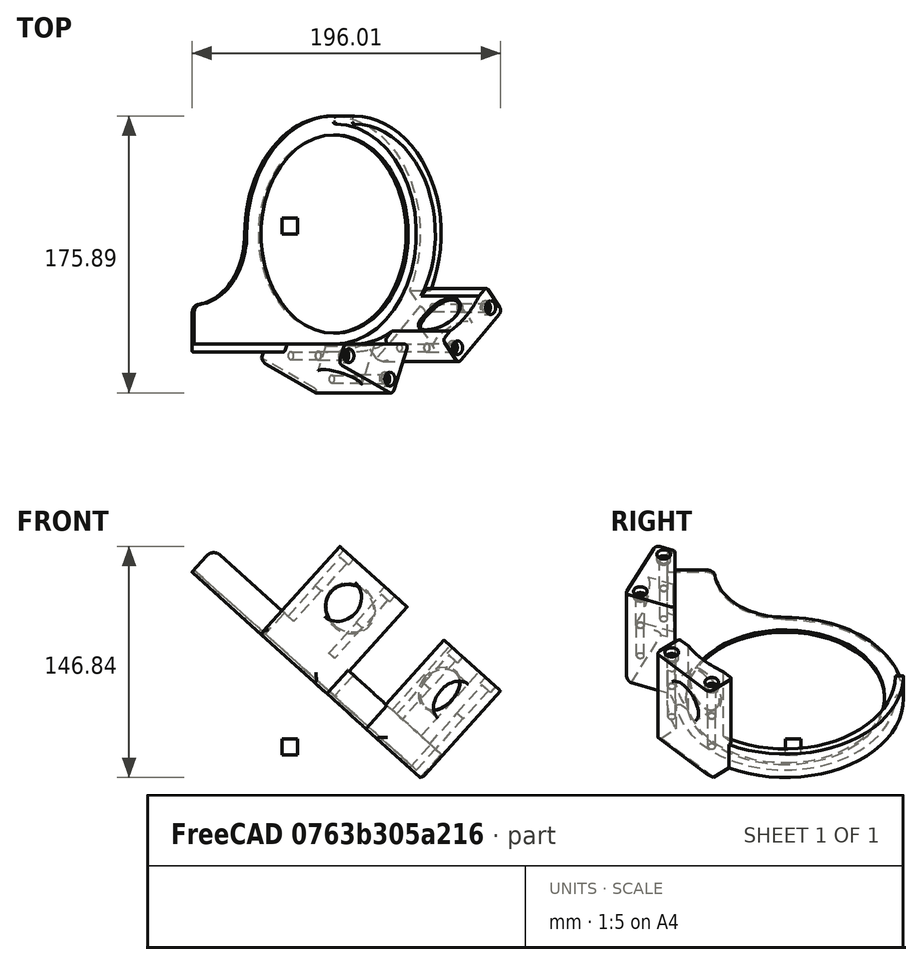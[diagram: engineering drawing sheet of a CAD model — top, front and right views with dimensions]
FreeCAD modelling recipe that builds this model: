
FCSTD DOCUMENT  (FreeCAD 0.19R)
Label: WhiteBike4
License: All rights reserved
LicenseURL: http://en.wikipedia.org/wiki/All_rights_reserved
objects: Sketcher::SketchObject×9, PartDesign::Fillet×7, PartDesign::Pocket×6, PartDesign::Pad×2, Mesh::Feature×2, PartDesign::Chamfer×1, PartDesign::Body×1, Part::Box×1
note: 43 computed .brp shape members not serialized (recipe doc carries the construction recipe); baked Part::Feature solids carry a one-line shape summary decoded from their .brp

FEATURE [Sketcher::SketchObject] Sketch
  FullyConstrained = true
  MapMode = 5
  Placement = pos=(45.5009,-1.12e-14,50.5338) rot=(0.93358,0,-0.358368;3.14159rad)
  sketch-geometry (5):
    g0: Circle CenterX=0 CenterY=0 CenterZ=0 NormalX=0 NormalY=0 NormalZ=1 AngleXU=0 Radius=63
    g1: ArcOfCircle CenterX=0 CenterY=0 CenterZ=0 NormalX=0 NormalY=0 NormalZ=1 AngleXU=0 Radius=75 StartAngle=3.14159 EndAngle=7.85398
    g2: LineSegment StartX=2.3e-14 StartY=75 StartZ=0 EndX=-120 EndY=75 EndZ=0
    g3: LineSegment StartX=-120 StartY=75 StartZ=0 EndX=-120 EndY=45 EndZ=0
    g4: ArcOfCircle CenterX=-120 CenterY=5.5e-15 CenterZ=0 NormalX=0 NormalY=0 NormalZ=1 AngleXU=0 Radius=45 StartAngle=0 EndAngle=1.5708
  constraints (14):
    c: Coincident(g0,g-1)
    c: Coincident(g1,g0)
    c: PointOnObject(g1,g-2)
    c: Coincident(g2,g1)
    c: Horizontal(g2)
    c: Coincident(g2,g3)
    c: Vertical(g3)
    c: Coincident(g4,g3)
    c: Tangent(g1,g4) = 1.5708
    c: Distance(g2) = 120
    c: Perpendicular(g4,g3)
    c: Radius(g0) = 63
    c: Radius(g1) = 75
    c: PointOnObject(g1,g-1)
FEATURE [PartDesign::Pad] Pad
  Direction = (1,1,1)
  Length = 20
  Length2 = 100
  Placement = pos=(45.5009,-1.12e-14,50.5338) rot=(0.93358,0,-0.358368;3.14159rad)
  Profile = -> Sketch
  Type = 0
FEATURE [Sketcher::SketchObject] Sketch002
  FullyConstrained = false
  MapMode = 5
  Placement = pos=(45.5009,-1.12e-14,50.5338) rot=(0,1,0;0.733038rad)
  Support = -> [Pad]
  sketch-geometry (10):
    g0: LineSegment StartX=0 StartY=0 StartZ=0 EndX=200.739 EndY=-222.943 EndZ=0
    g1: LineSegment StartX=-78.1462 StartY=-184.101 StartZ=0 EndX=0 EndY=0 EndZ=0
    g2: LineSegment StartX=-16.0605 StartY=-101.819 StartZ=0 EndX=-62.0857 EndY=-82.2822 EndZ=0
    g3: LineSegment StartX=-62.0857 StartY=-82.2822 StartZ=0 EndX=-54.2711 EndY=-63.8721 EndZ=0
    g4: LineSegment StartX=-54.2711 StartY=-63.8721 StartZ=0 EndX=-0.139101 EndY=-64.3103 EndZ=0
    g5: LineSegment StartX=-0.139101 StartY=-64.3103 StartZ=0 EndX=-16.0605 EndY=-101.819 EndZ=0
    g6: LineSegment StartX=77.4621 StartY=-48.6685 StartZ=0 EndX=40.3049 EndY=-82.125 EndZ=0
    g7: LineSegment StartX=40.3049 StartY=-82.125 StartZ=0 EndX=26.9223 EndY=-67.2621 EndZ=0
    g8: LineSegment StartX=26.9223 StartY=-67.2621 StartZ=0 EndX=64.0795 EndY=-33.8056 EndZ=0
    g9: LineSegment StartX=64.0795 StartY=-33.8056 StartZ=0 EndX=77.4621 EndY=-48.6685 EndZ=0
  constraints (27):
    c: Coincident(g0,g-1)
    c: Coincident(g1,g-1)
    c: Angle(g1) = 1.16937
    c: Distance(g1) = 200
    c: Distance(g0) = 300
    c: Coincident(g2,g3)
    c: Coincident(g3,g4)
    c: Coincident(g4,g5)
    c: Coincident(g5,g2)
    c: Coincident(g6,g7)
    c: Coincident(g7,g8)
    c: Coincident(g8,g9)
    c: Coincident(g9,g6)
    c: Equal(g8,g6)
    c: Perpendicular(g0,g8)
    c: Perpendicular(g9,g6)
    c: Symmetric(g6,g6,g0)
    c: Distance(g7) = 20
    c: Distance(g6) = 50
    c: Perpendicular(g3,g2)
    c: Perpendicular(g5,g2)
    c: Symmetric(g2,g2,g1)
    c: Distance(g3) = 20
    c: Distance(g2) = 50
    c: Angle(g1,g0) = 1.13446
    c: Distance(g-1,g8) = 68
    c: Distance(g-1,g2) = 100
FEATURE [PartDesign::Pad] Pad001
  BaseFeature = -> Pad
  Direction = (1,1,1)
  Length = 55
  Length2 = 20
  Placement = pos=(45.5009,-1.12e-14,50.5338) rot=(0.93358,0,-0.358368;3.14159rad)
  Profile = -> Sketch002
  Type = 4
FEATURE [Sketcher::SketchObject] Sketch001
  FullyConstrained = true
  MapMode = 5
  Placement = pos=(45.5009,-1.12e-14,50.5338) rot=(0,1,0;0.733038rad)
  Support = -> [Pad001]
  sketch-geometry (5):
    g0: ArcOfCircle CenterX=0 CenterY=0 CenterZ=0 NormalX=0 NormalY=0 NormalZ=1 AngleXU=0 Radius=70 StartAngle=4.71239 EndAngle=7.85398
    g1: LineSegment StartX=-180 StartY=95.72 StartZ=0 EndX=-180 EndY=-70 EndZ=0
    g2: LineSegment StartX=-180 StartY=-70 StartZ=0 EndX=0 EndY=-70 EndZ=0
    g3: LineSegment StartX=2.14e-14 StartY=70 StartZ=0 EndX=2.14e-14 EndY=95.72 EndZ=0
    g4: LineSegment StartX=2.14e-14 StartY=95.72 StartZ=0 EndX=-180 EndY=95.72 EndZ=0
  constraints (15):
    c: Coincident(g0,g-1)
    c: PointOnObject(g0,g-2)
    c: PointOnObject(g0,g-2)
    c: Radius(g0) = 70
    c: Vertical(g1)
    c: Coincident(g1,g2)
    c: Coincident(g2,g0)
    c: Horizontal(g2)
    c: Coincident(g0,g3)
    c: Coincident(g3,g4)
    c: Coincident(g4,g1)
    c: Horizontal(g4)
    c: Distance(g3) = 25.72
    c: Distance(g4) = 180
    c: Vertical(g3)
FEATURE [PartDesign::Pocket] Pocket
  BaseFeature = -> Pad001
  Length = 18
  Length2 = 100
  Placement = pos=(45.5009,-1.12e-14,50.5338) rot=(0.93358,0,-0.358368;3.14159rad)
  Profile = -> Sketch001
  Type = 4
FEATURE [Sketcher::SketchObject] Sketch007
  FullyConstrained = true
  MapMode = 5
  Placement = pos=(28.3992,9.76828,65.9323) rot=(-0.567561,-0.211541,0.795691;1.61766rad)
  Support = -> [Pocket]
  sketch-geometry (1):
    g0: Circle CenterX=0 CenterY=-30 CenterZ=0 NormalX=0 NormalY=0 NormalZ=1 AngleXU=0 Radius=13
  constraints (3):
    c: Radius(g0) = 13
    c: PointOnObject(g0,g-2)
    c: DistanceY(g0) = -30
FEATURE [Sketcher::SketchObject] Sketch008
  FullyConstrained = true
  MapMode = 5
  Placement = pos=(89.2598,-65.3967,11.1331) rot=(-0.473147,0.707107,-0.525483;3.14159rad)
  Support = -> [Pocket]
  sketch-geometry (1):
    g0: Circle CenterX=0 CenterY=-30 CenterZ=0 NormalX=0 NormalY=0 NormalZ=1 AngleXU=0 Radius=14.5
  constraints (3):
    c: Radius(g0) = 14.5
    c: PointOnObject(g0,g-2)
    c: DistanceY(g0) = -30
FEATURE [PartDesign::Pocket] Pocket001
  BaseFeature = -> Pocket
  Length = 5
  Length2 = 100
  Placement = pos=(45.5009,-1.12e-14,50.5338) rot=(0.93358,0,-0.358368;3.14159rad)
  Profile = -> Sketch008
  Type = 1
FEATURE [Sketcher::SketchObject] Sketch009
  FullyConstrained = true
  MapMode = 5
  Placement = pos=(16.4639,-92.0505,76.6789) rot=(0.126167,-0.644711,0.753943;2.36216rad)
  Support = -> [Pocket001]
  sketch-geometry (1):
    g0: Circle CenterX=0 CenterY=-30 CenterZ=0 NormalX=0 NormalY=0 NormalZ=1 AngleXU=0 Radius=14.5
  constraints (3):
    c: Radius(g0) = 14.5
    c: PointOnObject(g0,g-2)
    c: DistanceY(g0) = -30
FEATURE [PartDesign::Pocket] Pocket002
  BaseFeature = -> Pocket001
  Length = 5
  Length2 = 100
  Placement = pos=(45.5009,-1.12e-14,50.5338) rot=(0.93358,0,-0.358368;3.14159rad)
  Profile = -> Sketch009
  Type = 1
FEATURE [Sketcher::SketchObject] Sketch010
  ExternalGeometry = -> [Pocket002]
  FullyConstrained = true
  MapMode = 5
  Placement = pos=(82.3031,2.03e-14,91.4068) rot=(0,1,0;0.733038rad)
  Support = -> [Pocket002]
  sketch-geometry (4):
    g0: Circle CenterX=-53.4369 CenterY=-77.2626 CenterZ=0 NormalX=0 NormalY=0 NormalZ=1 AngleXU=0 Radius=2.4
    g1: Circle CenterX=-18.4577 CenterY=-92.1103 CenterZ=0 NormalX=0 NormalY=0 NormalZ=1 AngleXU=0 Radius=2.4
    g2: Circle CenterX=39.4107 CenterY=-72.1651 CenterZ=0 NormalX=0 NormalY=0 NormalZ=1 AngleXU=0 Radius=2.4
    g3: Circle CenterX=67.6502 CenterY=-46.7381 CenterZ=0 NormalX=0 NormalY=0 NormalZ=1 AngleXU=0 Radius=2.4
  constraints (12):
    c: Diameter(g0) = 4.8
    c: Equal(g0,g1)
    c: Equal(g0,g3)
    c: Equal(g0,g2)
    c: Distance(g1,g-7) = 6
    c: Distance(g0,g-6) = 6
    c: Distance(g2,g-5) = 6
    c: Distance(g3,g-3) = 6
    c: Distance(g3,g-4) = 8
    c: Distance(g2,g-4) = 8
    c: Distance(g1,g-8) = 8
    c: Distance(g0,g-8) = 8
FEATURE [PartDesign::Pocket] Pocket003
  BaseFeature = -> Pocket002
  Length = 55
  Length2 = 100
  Placement = pos=(45.5009,-1.12e-14,50.5338) rot=(0.93358,0,-0.358368;3.14159rad)
  Profile = -> Sketch010
  Type = 0
FEATURE [Sketcher::SketchObject] Sketch011
  ExternalGeometry = -> [Pocket003]
  FullyConstrained = true
  MapMode = 5
  Placement = pos=(82.3031,2.61e-14,91.4068) rot=(0,1,0;0.733038rad)
  Support = -> [Pocket003]
  sketch-geometry (4):
    g0: Circle CenterX=-53.4369 CenterY=-77.2626 CenterZ=0 NormalX=0 NormalY=0 NormalZ=1 AngleXU=0 Radius=4.35
    g1: Circle CenterX=-18.4577 CenterY=-92.1103 CenterZ=0 NormalX=0 NormalY=0 NormalZ=1 AngleXU=0 Radius=4.35
    g2: Circle CenterX=39.4107 CenterY=-72.1651 CenterZ=0 NormalX=0 NormalY=0 NormalZ=1 AngleXU=0 Radius=4.35
    g3: Circle CenterX=67.6502 CenterY=-46.7381 CenterZ=0 NormalX=0 NormalY=0 NormalZ=1 AngleXU=0 Radius=4.35
  constraints (8):
    c: Diameter(g0) = 8.7
    c: Equal(g0,g1)
    c: Equal(g0,g2)
    c: Equal(g0,g3)
    c: Coincident(g3,g-3)
    c: Coincident(g2,g-4)
    c: Coincident(g1,g-5)
    c: Coincident(g0,g-6)
FEATURE [PartDesign::Pocket] Pocket004
  BaseFeature = -> Pocket003
  Length = 5
  Length2 = 100
  Placement = pos=(45.5009,-1.12e-14,50.5338) rot=(0.93358,0,-0.358368;3.14159rad)
  Profile = -> Sketch011
  Type = 0
FEATURE [Sketcher::SketchObject] Sketch012
  ExternalGeometry = -> [Pocket004]
  FullyConstrained = true
  MapMode = 5
  Placement = pos=(82.3031,1.12e-14,91.4068) rot=(0,1,0;0.733038rad)
  Support = -> [Pocket004]
  sketch-geometry (4):
    g0: Circle CenterX=39.4107 CenterY=-72.1651 CenterZ=0 NormalX=0 NormalY=0 NormalZ=1 AngleXU=0 Radius=2.75
    g1: Circle CenterX=67.6502 CenterY=-46.7381 CenterZ=0 NormalX=0 NormalY=0 NormalZ=1 AngleXU=0 Radius=2.75
    g2: Circle CenterX=-18.4577 CenterY=-92.1103 CenterZ=0 NormalX=0 NormalY=0 NormalZ=1 AngleXU=0 Radius=2.75
    g3: Circle CenterX=-53.4369 CenterY=-77.2626 CenterZ=0 NormalX=0 NormalY=0 NormalZ=1 AngleXU=0 Radius=2.75
  constraints (8):
    c: Diameter(g2) = 5.5
    c: Equal(g2,g1)
    c: Equal(g2,g0)
    c: Equal(g2,g3)
    c: Coincident(g3,g-6)
    c: Coincident(g1,g-3)
    c: Coincident(g0,g-4)
    c: Coincident(g2,g-5)
FEATURE [PartDesign::Pocket] Pocket005
  BaseFeature = -> Pocket004
  Length = 29
  Length2 = 100
  Placement = pos=(45.5009,-1.12e-14,50.5338) rot=(0.93358,0,-0.358368;3.14159rad)
  Profile = -> Sketch012
  Type = 0
FEATURE [PartDesign::Chamfer] Chamfer
  Angle = 45
  Base = -> Pocket005 [Edge84,Edge44]
  BaseFeature = -> Pocket005
  ChamferType = 0
  FlipDirection = false
  Placement = pos=(45.5009,-1.12e-14,50.5338) rot=(0.93358,0,-0.358368;3.14159rad)
  Size = 4
  Size2 = 1
  SupportTransform = false
FEATURE [PartDesign::Fillet] Fillet
  Base = -> Chamfer [Edge91,Edge86,Edge103,Edge19,Edge11,Edge4]
  BaseFeature = -> Chamfer
  Placement = pos=(45.5009,-1.12e-14,50.5338) rot=(0.93358,0,-0.358368;3.14159rad)
  Radius = 3
  SupportTransform = false
FEATURE [PartDesign::Fillet] Fillet001
  Base = -> Fillet [Edge86,Edge67]
  BaseFeature = -> Fillet
  Placement = pos=(45.5009,-1.12e-14,50.5338) rot=(0.93358,0,-0.358368;3.14159rad)
  Radius = 6
  SupportTransform = false
FEATURE [PartDesign::Fillet] Fillet002
  Base = -> Fillet001 [Edge69]
  BaseFeature = -> Fillet001
  Placement = pos=(45.5009,-1.12e-14,50.5338) rot=(0.93358,0,-0.358368;3.14159rad)
  Radius = 1
  SupportTransform = false
FEATURE [PartDesign::Fillet] Fillet003
  Base = -> Fillet002 [Edge38,Edge104,Edge94,Edge34]
  BaseFeature = -> Fillet002
  Placement = pos=(45.5009,-1.12e-14,50.5338) rot=(0.93358,0,-0.358368;3.14159rad)
  Radius = 2
  SupportTransform = false
FEATURE [PartDesign::Fillet] Fillet004
  Base = -> Fillet003 [Face40]
  BaseFeature = -> Fillet003
  Placement = pos=(45.5009,-1.12e-14,50.5338) rot=(0.93358,0,-0.358368;3.14159rad)
  Radius = 1
  SupportTransform = false
FEATURE [PartDesign::Fillet] Fillet005
  Base = -> Fillet004 [Edge66]
  BaseFeature = -> Fillet004
  Placement = pos=(45.5009,-1.12e-14,50.5338) rot=(0.93358,0,-0.358368;3.14159rad)
  Radius = 1
  SupportTransform = false
FEATURE [PartDesign::Fillet] Fillet006
  Base = -> Fillet005 [Edge68,Edge136,Edge77,Edge22]
  BaseFeature = -> Fillet005
  Placement = pos=(45.5009,-1.12e-14,50.5338) rot=(0.93358,0,-0.358368;3.14159rad)
  Radius = 1
  SupportTransform = false
FEATURE [PartDesign::Body] Body
  Group = -> [Sketch,Sketch001,Sketch002,Sketch007,Pad,Pad001,Pocket,Sketch008,Pocket001,Sketch009,Pocket002,Sketch010,Pocket003,Sketch011,Pocket004,Sketch012,Pocket005,Chamfer,Fillet,Fillet001,Fillet002,Fillet003,Fillet004,Fillet005,Fillet006]
  Origin = -> Origin
  Tip = -> Fillet006
FEATURE [Mesh::Feature] Mesh  label="Fillet006 (Meshed)"
FEATURE [Part::Box] Box  label="Cube"
  AttacherType = Attacher::AttachEngine3D
  Height = 10
  Length = 10
  Width = 10
FEATURE [Mesh::Feature] Mesh001  label="Cube (Meshed)"
